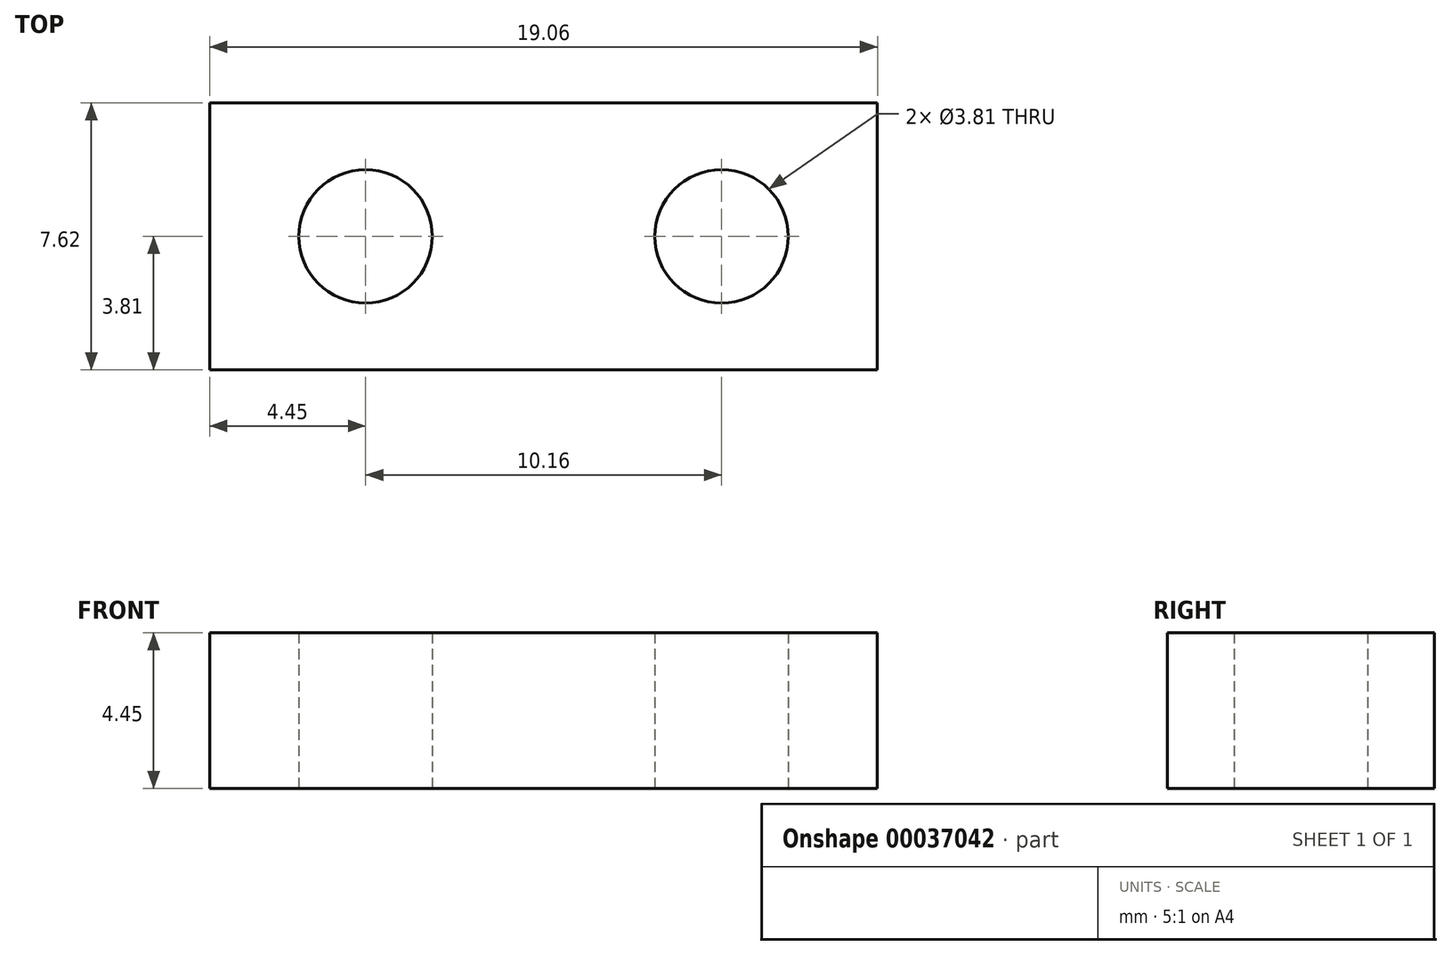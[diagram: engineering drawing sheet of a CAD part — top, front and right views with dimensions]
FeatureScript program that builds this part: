
annotation { "Feature Type Name" : "Feature", "Feature Type Description" : "" }
export const myFeature = defineFeature(function(context is Context, id is Id, definition is map)
    precondition{}
    {
        {
            var Q0;
            Q0=qCreatedBy(makeId("Top.planeOp"),FACE);
            var sketch = newSketch(context, id + "F0", { "sketchPlane" : qUnion([Q0])});
            skLineSegment(sketch, "E0.rect.bottom", {"start": v(9.53, 3.81) * mm, "end": v(-9.53, 3.8) * mm});
            skLineSegment(sketch, "E0.rect.top", {"start": v(9.53, -3.8) * mm, "end": v(-9.53, -3.81) * mm});
            skLineSegment(sketch, "E0.rect.left", {"start": v(9.53, 3.81) * mm, "end": v(9.53, -3.8) * mm});
            skLineSegment(sketch, "E0.rect.right", {"start": v(-9.53, 3.8) * mm, "end": v(-9.53, -3.81) * mm});
            skPoint(sketch, "E0.rect.middle", {"position": v(0, 0) * mm});
            skCircle(sketch, "E1", {"center": v(5.08, 0) * mm, "radius": 1.9 * mm});
            skCircle(sketch, "E2", {"center": v(-5.08, 0) * mm, "radius": 1.9 * mm});
            skLineSegment(sketch, "E3", {"start": v(-5.08, 0) * mm, "end": v(5.08, 0) * mm, "construction": true});
            skSolve(sketch);
        }
        {
            var Q0;
            Q0 = qSketchRegion(id + "F0", true);
            extrude(context, id + "F1", {"entities" : qUnion([Q0]), "depth" : 4.44 * mm});
        }
    });
